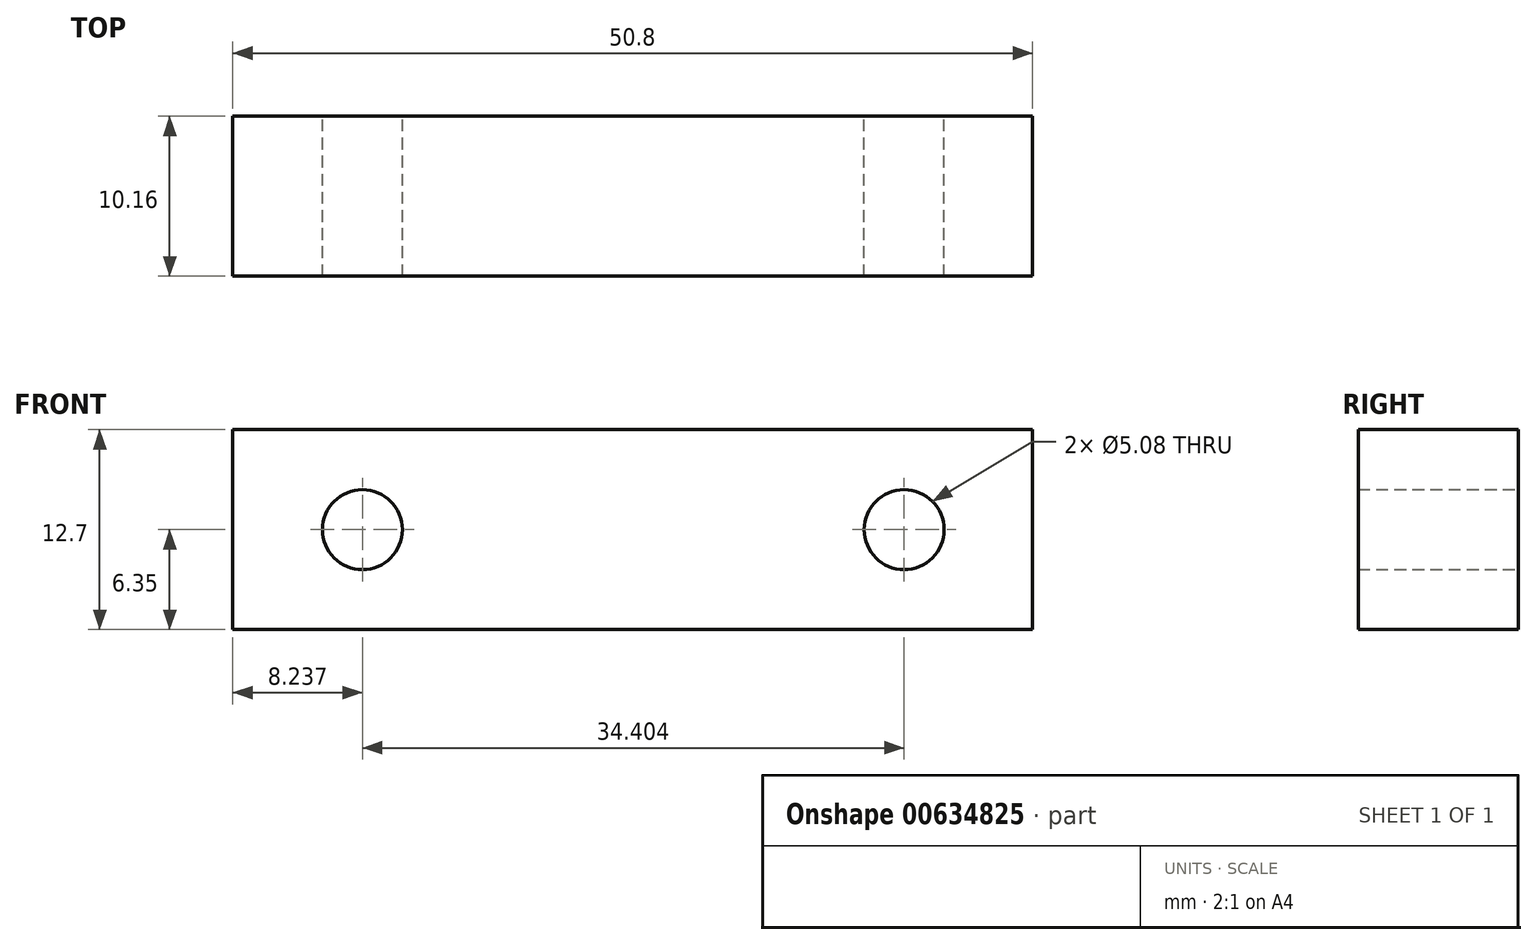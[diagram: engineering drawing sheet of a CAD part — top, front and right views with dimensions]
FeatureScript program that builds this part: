
annotation { "Feature Type Name" : "Feature", "Feature Type Description" : "" }
export const myFeature = defineFeature(function(context is Context, id is Id, definition is map)
    precondition{}
    {
        {
            var Q0;
            Q0=qCreatedBy(makeId("Front.planeOp"),FACE);
            var sketch = newSketch(context, id + "F0", { "sketchPlane" : qUnion([Q0])});
            skLineSegment(sketch, "E0.bottom", {"start": v(-25.4, 6.35) * mm, "end": v(25.4, 6.35) * mm});
            skLineSegment(sketch, "E0.top", {"start": v(-25.4, -6.35) * mm, "end": v(25.4, -6.35) * mm});
            skLineSegment(sketch, "E0.left", {"start": v(-25.4, 6.35) * mm, "end": v(-25.4, -6.35) * mm});
            skLineSegment(sketch, "E0.right", {"start": v(25.4, 6.35) * mm, "end": v(25.4, -6.35) * mm});
            skPoint(sketch, "E0.middle", {"position": v(0, 0) * mm});
            skCircle(sketch, "E1", {"center": v(17.24, 0) * mm, "radius": 2.54 * mm});
            skCircle(sketch, "E2", {"center": v(-17.16, 0) * mm, "radius": 2.54 * mm});
            skSolve(sketch);
        }
        {
            var Q0;
            Q0=makeQuery(id+"F0.imprint","IMPRINT",FACE,{"disambiguationData":[TD([[makeQuery(id+"F0.imprint","IMPRINT",EDGE,{"derivedFrom":sQuery(id+"F0.wireOp",EDGE,"E0.bottom")}),-1.0]])]});
            extrude(context, id + "F1", {"entities" : qUnion([Q0]), "endBound" : BoundingType.SYMMETRIC, "depth" : 10.16 * mm, "offsetDistance" : 25.4 * mm});
        }
    });
